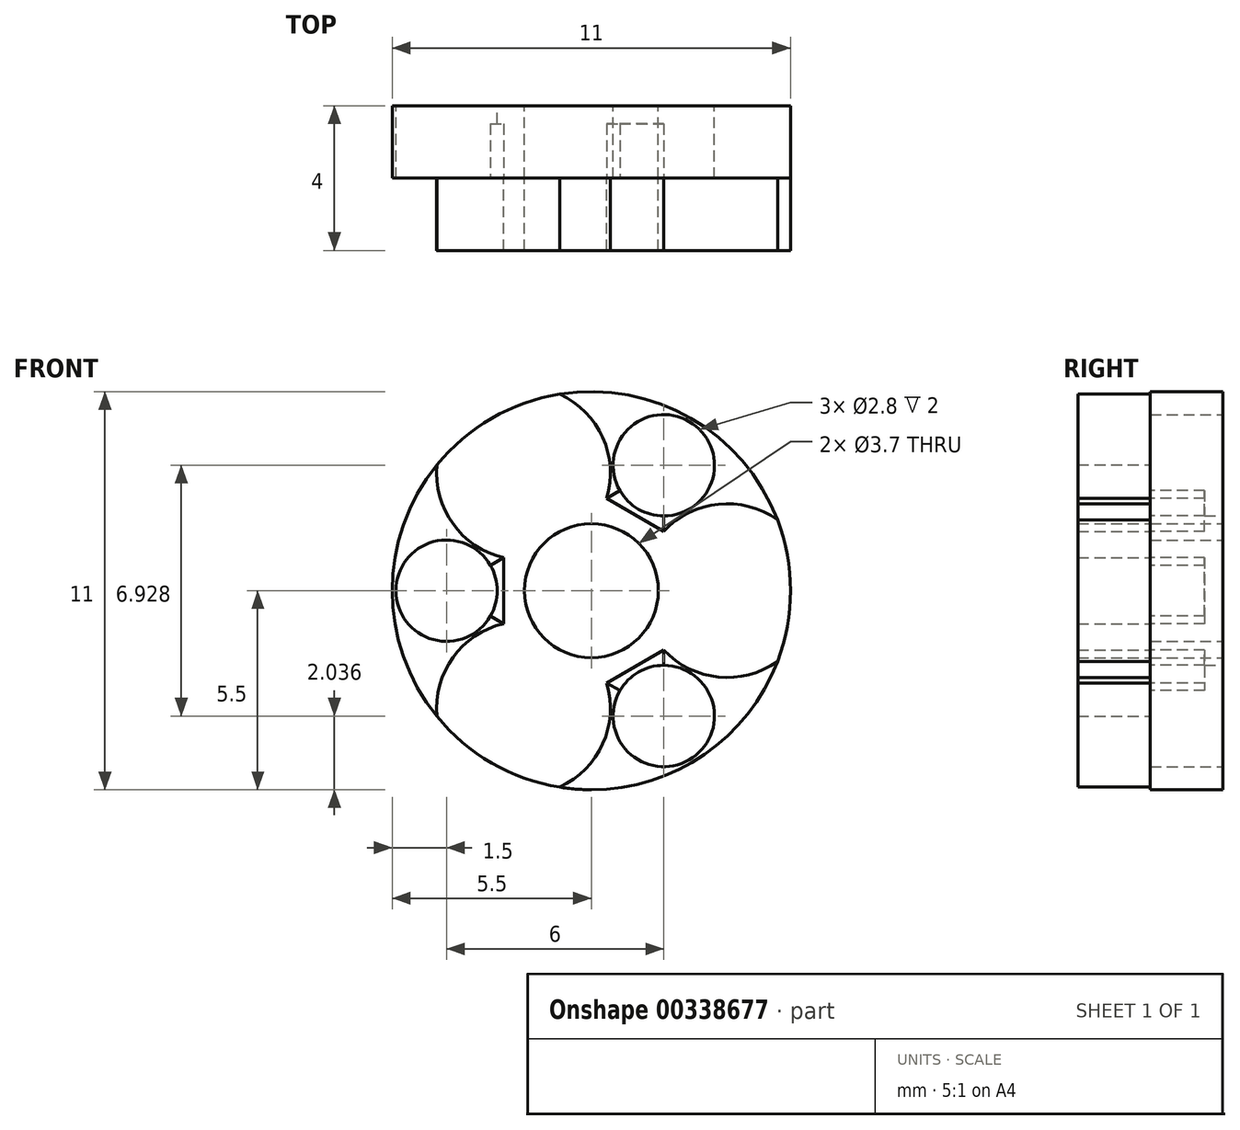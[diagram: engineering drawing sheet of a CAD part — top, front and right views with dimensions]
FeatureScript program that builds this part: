
annotation { "Feature Type Name" : "Feature", "Feature Type Description" : "" }
export const myFeature = defineFeature(function(context is Context, id is Id, definition is map)
    precondition{}
    {
        {
            var Q0;
            Q0=qCreatedBy(makeId("Front.planeOp"),FACE);
            var sketch = newSketch(context, id + "F0", { "sketchPlane" : qUnion([Q0])});
            skCircle(sketch, "E0", {"center": v(0, 0) * mm, "radius": 5.5 * mm});
            skCircle(sketch, "E1", {"center": v(0, 0) * mm, "radius": 1.85 * mm});
            skCircle(sketch, "E2.cCircle", {"center": v(0, 0) * mm, "radius": 4 * mm, "construction": true});
            skCircle(sketch, "E3", {"center": v(-4, 0) * mm, "radius": 1.4 * mm});
            skCircle(sketch, "E4", {"center": v(2, 3.46) * mm, "radius": 1.4 * mm});
            skCircle(sketch, "E5", {"center": v(2, -3.46) * mm, "radius": 1.4 * mm});
            skSolve(sketch);
        }
        {
            var Q0;
            Q0=makeQuery(id+"F0.imprint","IMPRINT",FACE,{"disambiguationData":[TD([[makeQuery(id+"F0.imprint","IMPRINT",EDGE,{"derivedFrom":sQuery(id+"F0.wireOp",EDGE,"E0")}),1.0]])]});
            extrude(context, id + "F1", {"entities" : qUnion([Q0]), "endBound" : BoundingType.SYMMETRIC, "depth" : 2 * mm});
        }
        {
            var Q0;
            Q0=makeQuery(id+"F1.opExtrude","CAP_FACE",FACE,{"disambiguationData":[OSD([sQuery(id+"F0.wireOp",EDGE,"E0"),sQuery(id+"F0.wireOp",EDGE,"E1"),sQuery(id+"F0.wireOp",EDGE,"E3"),sQuery(id+"F0.wireOp",EDGE,"E4"),sQuery(id+"F0.wireOp",EDGE,"E5")])],"isStart":false});
            var sketch = newSketch(context, id + "F2", { "sketchPlane" : qUnion([Q0])});
            skLineSegment(sketch, "E6", {"start": v(2, 3.46) * mm, "end": v(0, 0) * mm});
            skLineSegment(sketch, "E7", {"start": v(0, 0) * mm, "end": v(-4, 0) * mm});
            skLineSegment(sketch, "E8", {"start": v(-4, 0) * mm, "end": v(2, -3.46) * mm});
            skLineSegment(sketch, "E9", {"start": v(2, -3.46) * mm, "end": v(2, 3.46) * mm});
            skLineSegment(sketch, "E10", {"start": v(-4, 0) * mm, "end": v(2, 3.46) * mm});
            skLineSegment(sketch, "E11", {"start": v(-1, 1.73) * mm, "end": v(0, 0) * mm});
            skLineSegment(sketch, "E12", {"start": v(-1, 1.73) * mm, "end": v(-2.75, 4.76) * mm});
            skLineSegment(sketch, "E13", {"start": v(0, 0) * mm, "end": v(2, 0) * mm});
            skLineSegment(sketch, "E14", {"start": v(2, 0) * mm, "end": v(5.5, 0) * mm});
            skLineSegment(sketch, "E15", {"start": v(0, 0) * mm, "end": v(-1, -1.73) * mm});
            skLineSegment(sketch, "E16", {"start": v(-1, -1.73) * mm, "end": v(-2.75, -4.76) * mm});
            skCircle(sketch, "E17", {"center": v(-1.88, 3.25) * mm, "radius": 2.4 * mm});
            skCircle(sketch, "E18", {"center": v(-1.87, -3.25) * mm, "radius": 2.4 * mm});
            skCircle(sketch, "E19", {"center": v(3.75, 0) * mm, "radius": 2.4 * mm});
            skLineSegment(sketch, "E20", {"start": v(2, 1.64) * mm, "end": v(0.42, 2.55) * mm});
            skLineSegment(sketch, "E21", {"start": v(2, -1.64) * mm, "end": v(0.42, -2.55) * mm});
            skLineSegment(sketch, "E22", {"start": v(-2.42, 0.91) * mm, "end": v(-2.42, -0.91) * mm});
            skSolve(sketch);
        }
        {
            var Q0;
            {var subQ0=sQuery(id+"F2.wireOp",EDGE,"E12");Q0=makeQuery(id+"F2.imprint","IMPRINT",FACE,{"disambiguationData":[TD([[makeQuery(id+"F2.imprint","IMPRINT",EDGE,{"derivedFrom":subQ0}),-1.0]])]});}
            var Q1;
            {var subQ0=sQuery(id+"F2.wireOp",EDGE,"E12");Q1=makeQuery(id+"F2.imprint","IMPRINT",FACE,{"disambiguationData":[TD([[makeQuery(id+"F2.imprint","IMPRINT",EDGE,{"derivedFrom":subQ0}),1.0]])]});}
            var Q2;
            {var subQ0=sQuery(id+"F2.wireOp",EDGE,"E14");Q2=makeQuery(id+"F2.imprint","IMPRINT",FACE,{"disambiguationData":[TD([[makeQuery(id+"F2.imprint","IMPRINT",EDGE,{"derivedFrom":subQ0}),1.0]])]});}
            var Q3;
            {var subQ0=sQuery(id+"F2.wireOp",EDGE,"E14");Q3=makeQuery(id+"F2.imprint","IMPRINT",FACE,{"disambiguationData":[TD([[makeQuery(id+"F2.imprint","IMPRINT",EDGE,{"derivedFrom":subQ0}),-1.0]])]});}
            var Q4;
            {var subQ0=sQuery(id+"F2.wireOp",EDGE,"E16");Q4=makeQuery(id+"F2.imprint","IMPRINT",FACE,{"disambiguationData":[TD([[makeQuery(id+"F2.imprint","IMPRINT",EDGE,{"derivedFrom":subQ0}),1.0]])]});}
            var Q5;
            {var subQ0=sQuery(id+"F2.wireOp",EDGE,"E16");Q5=makeQuery(id+"F2.imprint","IMPRINT",FACE,{"disambiguationData":[TD([[makeQuery(id+"F2.imprint","IMPRINT",EDGE,{"derivedFrom":subQ0}),-1.0]])]});}
            var Q6;
            {var subQ0=sQuery(id+"F2.wireOp",EDGE,"E20");var subQ1=sQuery(id+"F2.wireOp",EDGE,"E6");var subQ2=makeQuery(id+"F2.imprint","INTERSECT",VERTEX,{"derivedFrom":[subQ1,subQ0]});Q6=makeQuery(id+"F2.imprint","IMPRINT",FACE,{"disambiguationData":[TD([[makeQuery(id+"F2.imprint","IMPRINT",EDGE,{"disambiguationData":[TD([[subQ2,-1.0]])],"derivedFrom":subQ1}),-1.0]])]});}
            var Q7;
            {var subQ0=sQuery(id+"F2.wireOp",EDGE,"E20");var subQ1=sQuery(id+"F2.wireOp",EDGE,"E6");var subQ2=makeQuery(id+"F2.imprint","INTERSECT",VERTEX,{"derivedFrom":[subQ1,subQ0]});Q7=makeQuery(id+"F2.imprint","IMPRINT",FACE,{"disambiguationData":[TD([[makeQuery(id+"F2.imprint","IMPRINT",EDGE,{"disambiguationData":[TD([[subQ2,-1.0]])],"derivedFrom":subQ1}),1.0]])]});}
            var Q8;
            {var subQ0=sQuery(id+"F2.wireOp",EDGE,"E21");Q8=makeQuery(id+"F2.imprint","IMPRINT",FACE,{"disambiguationData":[TD([[makeQuery(id+"F2.imprint","IMPRINT",EDGE,{"derivedFrom":subQ0}),-1.0]])]});}
            var Q9;
            {var subQ0=sQuery(id+"F2.wireOp",EDGE,"E22");var subQ1=sQuery(id+"F2.wireOp",EDGE,"E7");var subQ2=makeQuery(id+"F2.imprint","INTERSECT",VERTEX,{"derivedFrom":[subQ1,subQ0]});Q9=makeQuery(id+"F2.imprint","IMPRINT",FACE,{"disambiguationData":[TD([[makeQuery(id+"F2.imprint","IMPRINT",EDGE,{"disambiguationData":[TD([[subQ2,1.0]])],"derivedFrom":subQ1}),-1.0]])]});}
            var Q10;
            {var subQ0=sQuery(id+"F2.wireOp",EDGE,"E22");var subQ1=sQuery(id+"F2.wireOp",EDGE,"E7");var subQ2=makeQuery(id+"F2.imprint","INTERSECT",VERTEX,{"derivedFrom":[subQ1,subQ0]});Q10=makeQuery(id+"F2.imprint","IMPRINT",FACE,{"disambiguationData":[TD([[makeQuery(id+"F2.imprint","IMPRINT",EDGE,{"disambiguationData":[TD([[subQ2,1.0]])],"derivedFrom":subQ1}),1.0]])]});}
            var Q11;
            {var subQ0=sQuery(id+"F2.wireOp",EDGE,"E11");var subQ5=makeQuery(id+"F1.opExtrude","CAP_EDGE",EDGE,{"disambiguationData":[OSD([sQuery(id+"F0.wireOp",EDGE,"E1")])],"isStart":false});var subQ7=makeQuery(id+"F2.imprint","INTERSECT",VERTEX,{"derivedFrom":[subQ5,subQ0]});Q11=makeQuery(id+"F2.imprint","IMPRINT",FACE,{"disambiguationData":[TD([[makeQuery(id+"F2.imprint","IMPRINT",EDGE,{"disambiguationData":[TD([[subQ7,1.0]])],"derivedFrom":subQ5}),-1.0]])]});}
            var Q12;
            {var subQ0=sQuery(id+"F2.wireOp",EDGE,"E11");var subQ5=makeQuery(id+"F1.opExtrude","CAP_EDGE",EDGE,{"disambiguationData":[OSD([sQuery(id+"F0.wireOp",EDGE,"E1")])],"isStart":false});var subQ6=makeQuery(id+"F2.imprint","INTERSECT",VERTEX,{"derivedFrom":[subQ5,subQ0]});Q12=makeQuery(id+"F2.imprint","IMPRINT",FACE,{"disambiguationData":[TD([[makeQuery(id+"F2.imprint","IMPRINT",EDGE,{"disambiguationData":[TD([[subQ6,-1.0]])],"derivedFrom":subQ5}),-1.0]])]});}
            var Q13;
            {var subQ0=sQuery(id+"F2.wireOp",EDGE,"E15");var subQ5=makeQuery(id+"F1.opExtrude","CAP_EDGE",EDGE,{"disambiguationData":[OSD([sQuery(id+"F0.wireOp",EDGE,"E1")])],"isStart":false});var subQ6=makeQuery(id+"F2.imprint","INTERSECT",VERTEX,{"derivedFrom":[subQ5,subQ0]});Q13=makeQuery(id+"F2.imprint","IMPRINT",FACE,{"disambiguationData":[TD([[makeQuery(id+"F2.imprint","IMPRINT",EDGE,{"disambiguationData":[TD([[subQ6,1.0]])],"derivedFrom":subQ5}),-1.0]])]});}
            var Q14;
            {var subQ0=sQuery(id+"F2.wireOp",EDGE,"E15");var subQ5=makeQuery(id+"F1.opExtrude","CAP_EDGE",EDGE,{"disambiguationData":[OSD([sQuery(id+"F0.wireOp",EDGE,"E1")])],"isStart":false});var subQ6=makeQuery(id+"F2.imprint","INTERSECT",VERTEX,{"derivedFrom":[subQ5,subQ0]});Q14=makeQuery(id+"F2.imprint","IMPRINT",FACE,{"disambiguationData":[TD([[makeQuery(id+"F2.imprint","IMPRINT",EDGE,{"disambiguationData":[TD([[subQ6,-1.0]])],"derivedFrom":subQ5}),-1.0]])]});}
            var Q15;
            {var subQ0=sQuery(id+"F2.wireOp",EDGE,"E13");var subQ5=makeQuery(id+"F1.opExtrude","CAP_EDGE",EDGE,{"disambiguationData":[OSD([sQuery(id+"F0.wireOp",EDGE,"E1")])],"isStart":false});var subQ7=makeQuery(id+"F2.imprint","INTERSECT",VERTEX,{"derivedFrom":[subQ5,subQ0]});Q15=makeQuery(id+"F2.imprint","IMPRINT",FACE,{"disambiguationData":[TD([[makeQuery(id+"F2.imprint","IMPRINT",EDGE,{"disambiguationData":[TD([[subQ7,1.0]])],"derivedFrom":subQ5}),-1.0]])]});}
            var Q16;
            {var subQ0=sQuery(id+"F2.wireOp",EDGE,"E13");var subQ5=makeQuery(id+"F1.opExtrude","CAP_EDGE",EDGE,{"disambiguationData":[OSD([sQuery(id+"F0.wireOp",EDGE,"E1")])],"isStart":false});var subQ6=makeQuery(id+"F2.imprint","INTERSECT",VERTEX,{"derivedFrom":[subQ5,subQ0]});Q16=makeQuery(id+"F2.imprint","IMPRINT",FACE,{"disambiguationData":[TD([[makeQuery(id+"F2.imprint","IMPRINT",EDGE,{"disambiguationData":[TD([[subQ6,-1.0]])],"derivedFrom":subQ5}),-1.0]])]});}
            extrude(context, id + "F3", {"entities" : qUnion([Q0, Q1, Q2, Q3, Q4, Q5, Q6, Q7, Q8, Q9, Q10, Q11, Q12, Q13, Q14, Q15, Q16]), "depth" : 2 * mm});
        }
        {
            var Q0;
            {var subQ0=sQuery(id+"F2.wireOp",EDGE,"E20");var subQ1=sQuery(id+"F2.wireOp",EDGE,"E6");var subQ2=makeQuery(id+"F2.imprint","INTERSECT",VERTEX,{"derivedFrom":[subQ1,subQ0]});Q0=makeQuery(id+"F2.imprint","IMPRINT",FACE,{"disambiguationData":[TD([[makeQuery(id+"F2.imprint","IMPRINT",EDGE,{"disambiguationData":[TD([[subQ2,1.0]])],"derivedFrom":subQ1}),-1.0]])]});}
            var Q1;
            {var subQ0=sQuery(id+"F2.wireOp",EDGE,"E20");var subQ1=sQuery(id+"F2.wireOp",EDGE,"E6");var subQ2=makeQuery(id+"F2.imprint","INTERSECT",VERTEX,{"derivedFrom":[subQ1,subQ0]});Q1=makeQuery(id+"F2.imprint","IMPRINT",FACE,{"disambiguationData":[TD([[makeQuery(id+"F2.imprint","IMPRINT",EDGE,{"disambiguationData":[TD([[subQ2,1.0]])],"derivedFrom":subQ1}),1.0]])]});}
            var Q2;
            {var subQ0=sQuery(id+"F2.wireOp",EDGE,"E21");Q2=makeQuery(id+"F2.imprint","IMPRINT",FACE,{"disambiguationData":[TD([[makeQuery(id+"F2.imprint","IMPRINT",EDGE,{"derivedFrom":subQ0}),1.0]])]});}
            var Q3;
            {var subQ0=sQuery(id+"F2.wireOp",EDGE,"E22");var subQ1=sQuery(id+"F2.wireOp",EDGE,"E7");var subQ2=makeQuery(id+"F2.imprint","INTERSECT",VERTEX,{"derivedFrom":[subQ1,subQ0]});Q3=makeQuery(id+"F2.imprint","IMPRINT",FACE,{"disambiguationData":[TD([[makeQuery(id+"F2.imprint","IMPRINT",EDGE,{"disambiguationData":[TD([[subQ2,-1.0]])],"derivedFrom":subQ1}),1.0]])]});}
            var Q4;
            {var subQ0=sQuery(id+"F2.wireOp",EDGE,"E22");var subQ1=sQuery(id+"F2.wireOp",EDGE,"E7");var subQ2=makeQuery(id+"F2.imprint","INTERSECT",VERTEX,{"derivedFrom":[subQ1,subQ0]});Q4=makeQuery(id+"F2.imprint","IMPRINT",FACE,{"disambiguationData":[TD([[makeQuery(id+"F2.imprint","IMPRINT",EDGE,{"disambiguationData":[TD([[subQ2,-1.0]])],"derivedFrom":subQ1}),-1.0]])]});}
            extrude(context, id + "F4", {"entities" : qUnion([Q0, Q1, Q2, Q3, Q4]), "operationType" : NewBodyOperationType.REMOVE, "oppositeDirection" : true, "depth" : 1.5 * mm});
        }
    });
